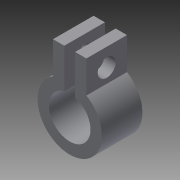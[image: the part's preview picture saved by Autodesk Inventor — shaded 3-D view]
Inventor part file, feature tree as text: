
AUTODESK INVENTOR PART (.ipt)
format: ipt  version: 2014 (Build 180170000, 170)  size: 108,032 bytes
history: native  units: in
note: dims shown in document units (in); Inventor stores cm internally (conversion verified against a paired STEP export)
features: extrude x2, sketch x2
ambient origin geometry x8: Origin, YZ Plane, XZ Plane, XY Plane, X Axis, Y Axis, Z Axis, Center Point
bodies: Solid1 (feature_tree)
feature tree (4):
  extrude  "Extrusion1"  Depth=0.0787in
  extrude  "Extrusion2"  Depth=0.075in
  sketch  "Sketch1"  dims[d6=0.2894in d12=0.0787in]
  sketch  "Sketch3"  dims[d13=0.0787in d14=0.075in d15=0.0375in d16=0.3353in d17=0.4144in d18=0.4144in d19=0.2825in d20=0.0in d25=0.125in d27=0.1412in d28=0.2894in d29=0.2825in d30=0.2325in d31=0.0in d32=0.0787in]
